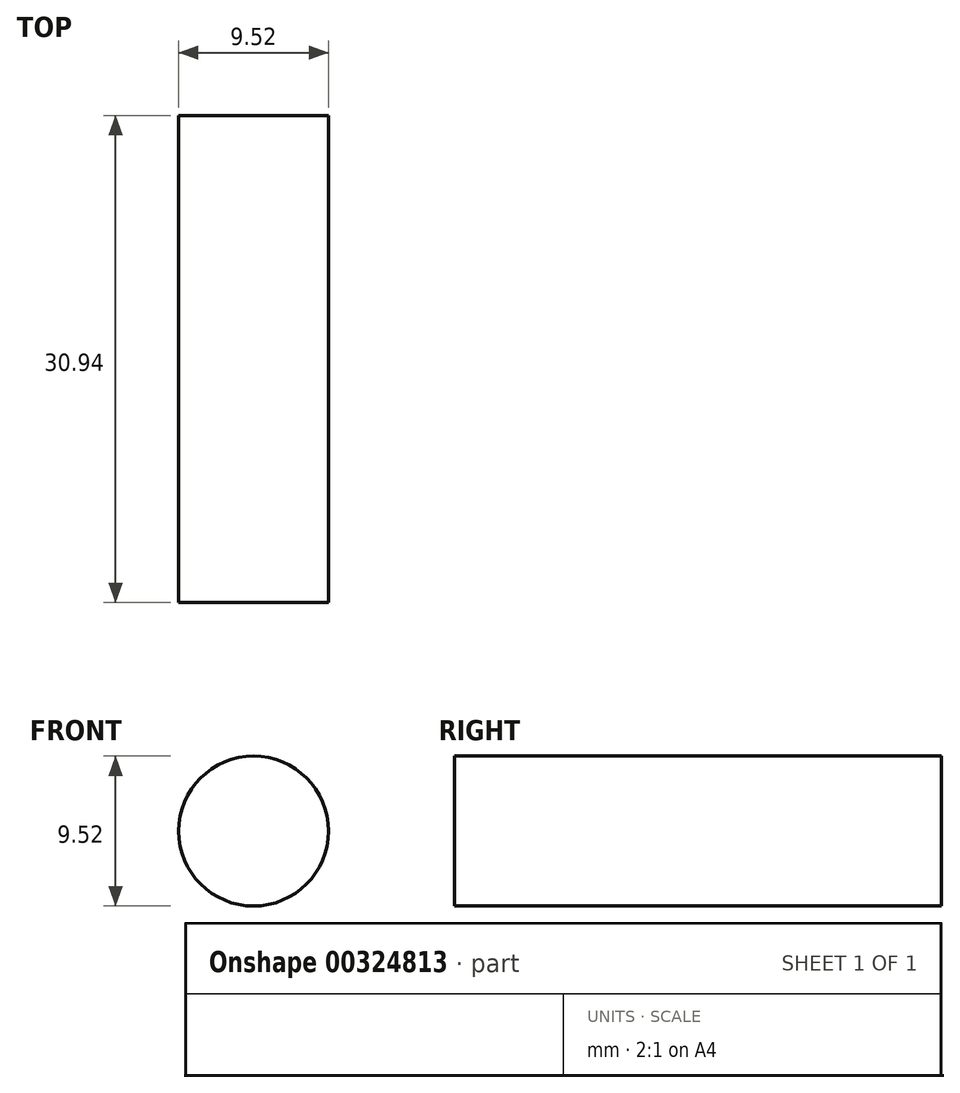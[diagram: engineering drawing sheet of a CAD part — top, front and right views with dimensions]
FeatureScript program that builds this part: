
annotation { "Feature Type Name" : "Feature", "Feature Type Description" : "" }
export const myFeature = defineFeature(function(context is Context, id is Id, definition is map)
    precondition{}
    {
        {
            var Q0;
            Q0=qCreatedBy(makeId("Front.planeOp"),FACE);
            var sketch = newSketch(context, id + "F0", { "sketchPlane" : qUnion([Q0])});
            skCircle(sketch, "E0", {"center": v(0, 0) * mm, "radius": 4.76 * mm});
            skSolve(sketch);
        }
        {
            var Q0;
            Q0=makeQuery(id+"F0.imprint","IMPRINT",FACE,{"disambiguationData":[TD([[makeQuery(id+"F0.imprint","IMPRINT",EDGE,{"derivedFrom":sQuery(id+"F0.wireOp",EDGE,"E0")}),1.0]])]});
            extrude(context, id + "F1", {"entities" : qUnion([Q0]), "depth" : 30.94 * mm, "offsetDistance" : 25.4 * mm});
        }
    });
